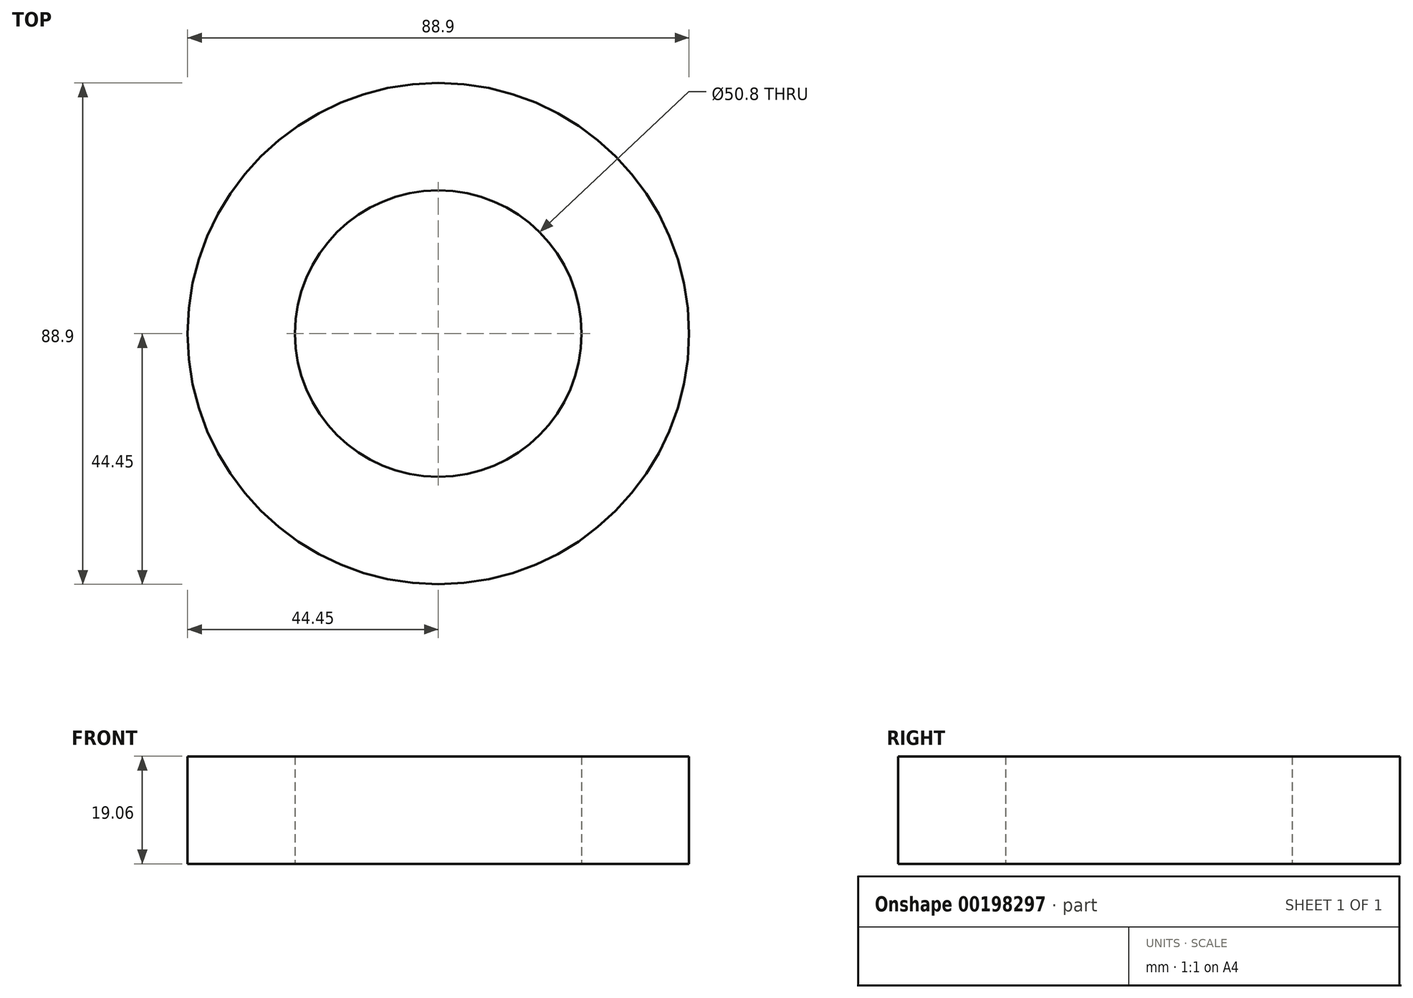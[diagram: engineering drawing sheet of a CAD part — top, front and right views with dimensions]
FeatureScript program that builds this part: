
annotation { "Feature Type Name" : "Feature", "Feature Type Description" : "" }
export const myFeature = defineFeature(function(context is Context, id is Id, definition is map)
    precondition{}
    {
        {
            var Q0;
            Q0=qCreatedBy(makeId("Top.planeOp"),FACE);
            var sketch = newSketch(context, id + "F0", { "sketchPlane" : qUnion([Q0])});
            skCircle(sketch, "E0", {"center": v(0, 0) * mm, "radius": 44.45 * mm});
            skCircle(sketch, "E1.0", {"center": v(0, 0) * mm, "radius": 25.4 * mm});
            skSolve(sketch);
        }
        {
            var Q0;
            Q0=makeQuery(id+"F0.imprint","IMPRINT",FACE,{"disambiguationData":[TD([[makeQuery(id+"F0.imprint","IMPRINT",EDGE,{"derivedFrom":sQuery(id+"F0.wireOp",EDGE,"E0")}),1.0]])]});
            extrude(context, id + "F1", {"entities" : qUnion([Q0]), "endBound" : BoundingType.SYMMETRIC, "depth" : 19.05 * mm});
        }
    });
